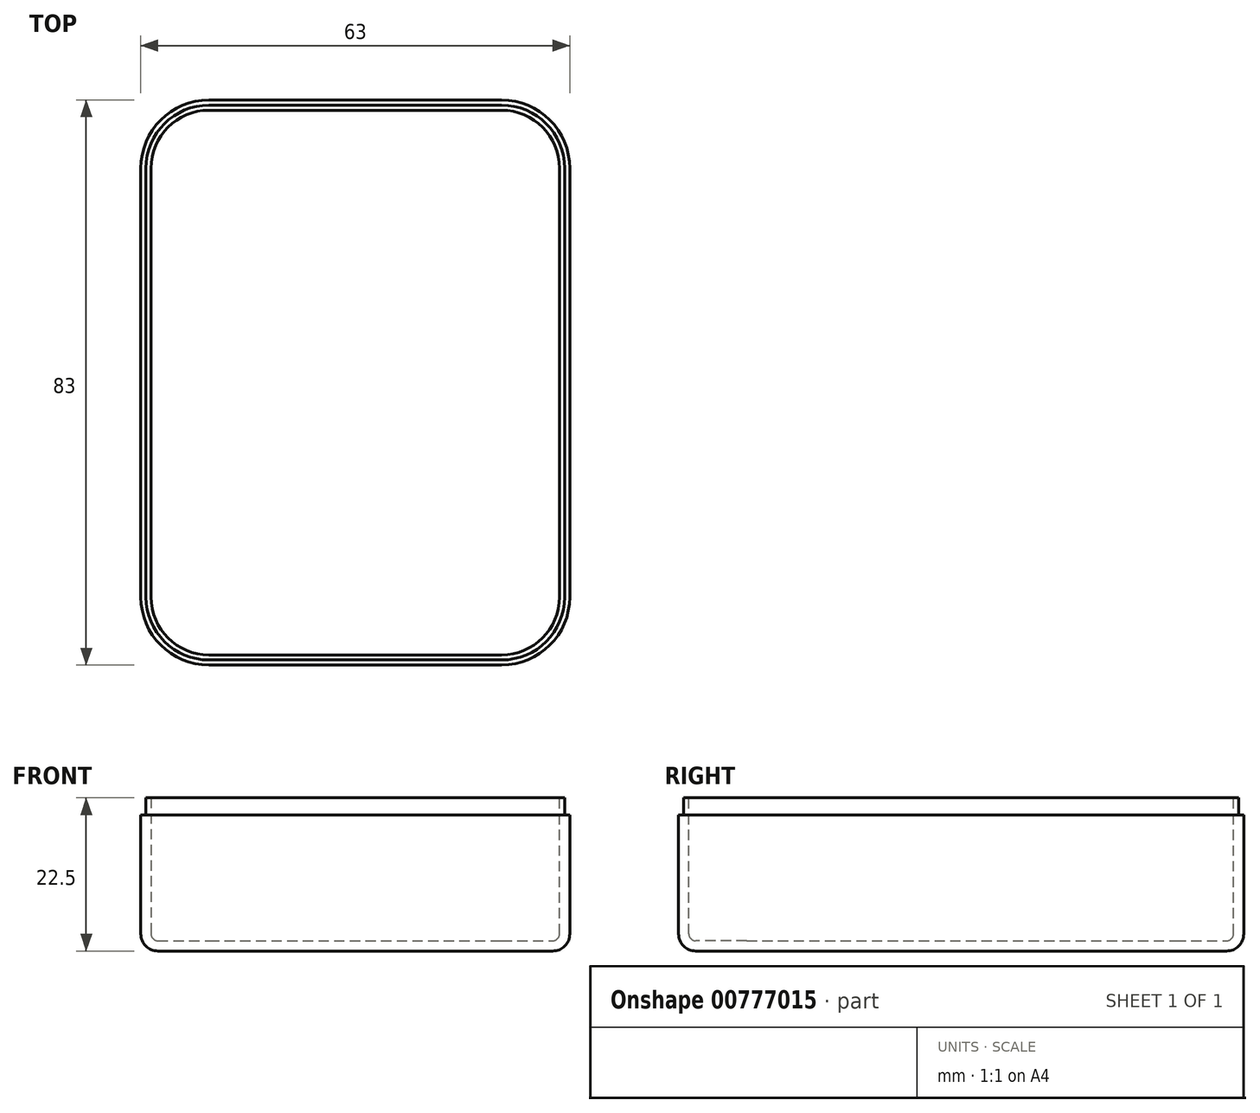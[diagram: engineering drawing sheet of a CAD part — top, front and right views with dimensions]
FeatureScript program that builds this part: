
annotation { "Feature Type Name" : "Feature", "Feature Type Description" : "" }
export const myFeature = defineFeature(function(context is Context, id is Id, definition is map)
    precondition{}
    {
        {
            var Q0;
            Q0=qCreatedBy(makeId("Top.planeOp"),FACE);
            var sketch = newSketch(context, id + "F0", { "sketchPlane" : qUnion([Q0])});
            skLineSegment(sketch, "E0.bottom", {"start": v(-59.26, 52.94) * mm, "end": v(-16.26, 52.94) * mm});
            skLineSegment(sketch, "E0.top", {"start": v(-59.26, -30.06) * mm, "end": v(-16.26, -30.06) * mm});
            skLineSegment(sketch, "E0.left", {"start": v(-69.26, 42.94) * mm, "end": v(-69.26, -20.06) * mm});
            skLineSegment(sketch, "E0.right", {"start": v(-6.26, 42.94) * mm, "end": v(-6.26, -20.06) * mm});
            skPoint(sketch, "E1.visualSharp", {"position": v(-69.26, 52.94) * mm});
            skArc(sketch, "E1.filletArc", {"start": v(-59.26, 52.94) * mm, "mid": v(-66.33, 50) * mm, "end": v(-69.26, 42.94) * mm});
            skPoint(sketch, "E2.visualSharp", {"position": v(-6.26, 52.94) * mm});
            skArc(sketch, "E2.filletArc", {"start": v(-6.26, 42.94) * mm, "mid": v(-9.19, 50) * mm, "end": v(-16.26, 52.94) * mm});
            skPoint(sketch, "E3.visualSharp", {"position": v(-6.26, -30.06) * mm});
            skArc(sketch, "E3.filletArc", {"start": v(-16.26, -30.06) * mm, "mid": v(-9.19, -27.13) * mm, "end": v(-6.26, -20.06) * mm});
            skPoint(sketch, "E4.visualSharp", {"position": v(-69.26, -30.06) * mm});
            skArc(sketch, "E4.filletArc", {"start": v(-69.26, -20.06) * mm, "mid": v(-66.33, -27.13) * mm, "end": v(-59.26, -30.06) * mm});
            skSolve(sketch);
        }
        {
            var Q0;
            Q0 = qSketchRegion(id + "F0", true);
            extrude(context, id + "F1", {"entities" : qUnion([Q0]), "flatOperationType" : FlatOperationType.REMOVE, "depth" : 20 * mm, "offsetDistance" : 25 * mm, "domain" : OperationDomain.MODEL});
        }
        {
            var Q0;
            Q0=makeQuery(id+"F1.opExtrude","CAP_FACE",FACE,{"disambiguationData":[OSD([sQuery(id+"F0.wireOp",EDGE,"E0.bottom"),sQuery(id+"F0.wireOp",EDGE,"E0.top"),sQuery(id+"F0.wireOp",EDGE,"E0.left"),sQuery(id+"F0.wireOp",EDGE,"E0.right"),sQuery(id+"F0.wireOp",EDGE,"E1.filletArc"),sQuery(id+"F0.wireOp",EDGE,"E2.filletArc"),sQuery(id+"F0.wireOp",EDGE,"E3.filletArc"),sQuery(id+"F0.wireOp",EDGE,"E4.filletArc")])],"isStart":true});
            fillet(context, id + "F2", {"entities" : qUnion([Q0]), "radius" : 2.5 * mm, "tangentPropagation" : true, "allowEdgeOverflow" : false});
        }
        {
            var Q0;
            Q0=makeQuery(id+"F1.opExtrude","CAP_FACE",FACE,{"disambiguationData":[OSD([sQuery(id+"F0.wireOp",EDGE,"E0.bottom"),sQuery(id+"F0.wireOp",EDGE,"E0.top"),sQuery(id+"F0.wireOp",EDGE,"E0.left"),sQuery(id+"F0.wireOp",EDGE,"E0.right"),sQuery(id+"F0.wireOp",EDGE,"E1.filletArc"),sQuery(id+"F0.wireOp",EDGE,"E2.filletArc"),sQuery(id+"F0.wireOp",EDGE,"E3.filletArc"),sQuery(id+"F0.wireOp",EDGE,"E4.filletArc")])],"isStart":false});
            shell(context, id + "F3", {"entities" : qUnion([Q0]), "thickness" : 1.5 * mm});
        }
        {
            var Q0;
            Q0=makeQuery(id+"F1.opExtrude","CAP_FACE",FACE,{"disambiguationData":[OSD([sQuery(id+"F0.wireOp",EDGE,"E0.bottom"),sQuery(id+"F0.wireOp",EDGE,"E0.left"),sQuery(id+"F0.wireOp",EDGE,"E0.right"),sQuery(id+"F0.wireOp",EDGE,"E1.filletArc"),sQuery(id+"F0.wireOp",EDGE,"E2.filletArc"),sQuery(id+"F0.wireOp",EDGE,"E3.filletArc"),sQuery(id+"F0.wireOp",EDGE,"E4.filletArc"),sQuery(id+"F0.wireOp",EDGE,"d9edf215-bd34-4b25-a5de-3ec3039a00d7.direction1")])],"isStart":false});
            var sketch = newSketch(context, id + "F4", { "sketchPlane" : qUnion([Q0])});
            skLineSegment(sketch, "E5.0", {"start": v(-7.76, 42.94) * mm, "end": v(-7.76, -20.06) * mm});
            skLineSegment(sketch, "E5.1", {"start": v(-59.26, 51.44) * mm, "end": v(-16.26, 51.44) * mm});
            skArc(sketch, "E5.2", {"start": v(-7.76, 42.94) * mm, "mid": v(-10.25, 48.95) * mm, "end": v(-16.26, 51.44) * mm});
            skArc(sketch, "E5.3", {"start": v(-59.26, 51.44) * mm, "mid": v(-65.27, 48.95) * mm, "end": v(-67.76, 42.94) * mm});
            skLineSegment(sketch, "E5.4", {"start": v(-67.76, 42.94) * mm, "end": v(-67.76, -20.06) * mm});
            skArc(sketch, "E5.5", {"start": v(-67.76, -20.06) * mm, "mid": v(-65.27, -26.07) * mm, "end": v(-59.26, -28.56) * mm});
            skArc(sketch, "E5.6", {"start": v(-16.26, -28.56) * mm, "mid": v(-10.25, -26.07) * mm, "end": v(-7.76, -20.06) * mm});
            skLineSegment(sketch, "E5.7", {"start": v(-59.26, -28.56) * mm, "end": v(-16.26, -28.56) * mm});
            skArc(sketch, "E6.0", {"start": v(-68.5, -20.06) * mm, "mid": v(-65.8, -26.6) * mm, "end": v(-59.26, -29.31) * mm});
            skLineSegment(sketch, "E6.1", {"start": v(-68.5, 42.94) * mm, "end": v(-68.5, -20.06) * mm});
            skLineSegment(sketch, "E6.2", {"start": v(-59.26, -29.31) * mm, "end": v(-16.26, -29.31) * mm});
            skArc(sketch, "E6.3", {"start": v(-59.26, 52.19) * mm, "mid": v(-65.8, 49.48) * mm, "end": v(-68.5, 42.94) * mm});
            skArc(sketch, "E6.4", {"start": v(-16.26, -29.31) * mm, "mid": v(-9.72, -26.6) * mm, "end": v(-7, -20.06) * mm});
            skLineSegment(sketch, "E6.5", {"start": v(-7, 42.94) * mm, "end": v(-7, -20.06) * mm});
            skArc(sketch, "E6.6", {"start": v(-7, 42.94) * mm, "mid": v(-9.72, 49.48) * mm, "end": v(-16.26, 52.19) * mm});
            skLineSegment(sketch, "E6.7", {"start": v(-59.26, 52.19) * mm, "end": v(-16.26, 52.19) * mm});
            skSolve(sketch);
        }
        {
            var Q0;
            Q0 = qSketchRegion(id + "F4", true);
            extrude(context, id + "F5", {"entities" : qUnion([Q0]), "operationType" : NewBodyOperationType.ADD, "depth" : 2.5 * mm, "offsetDistance" : 25 * mm});
        }
    });
